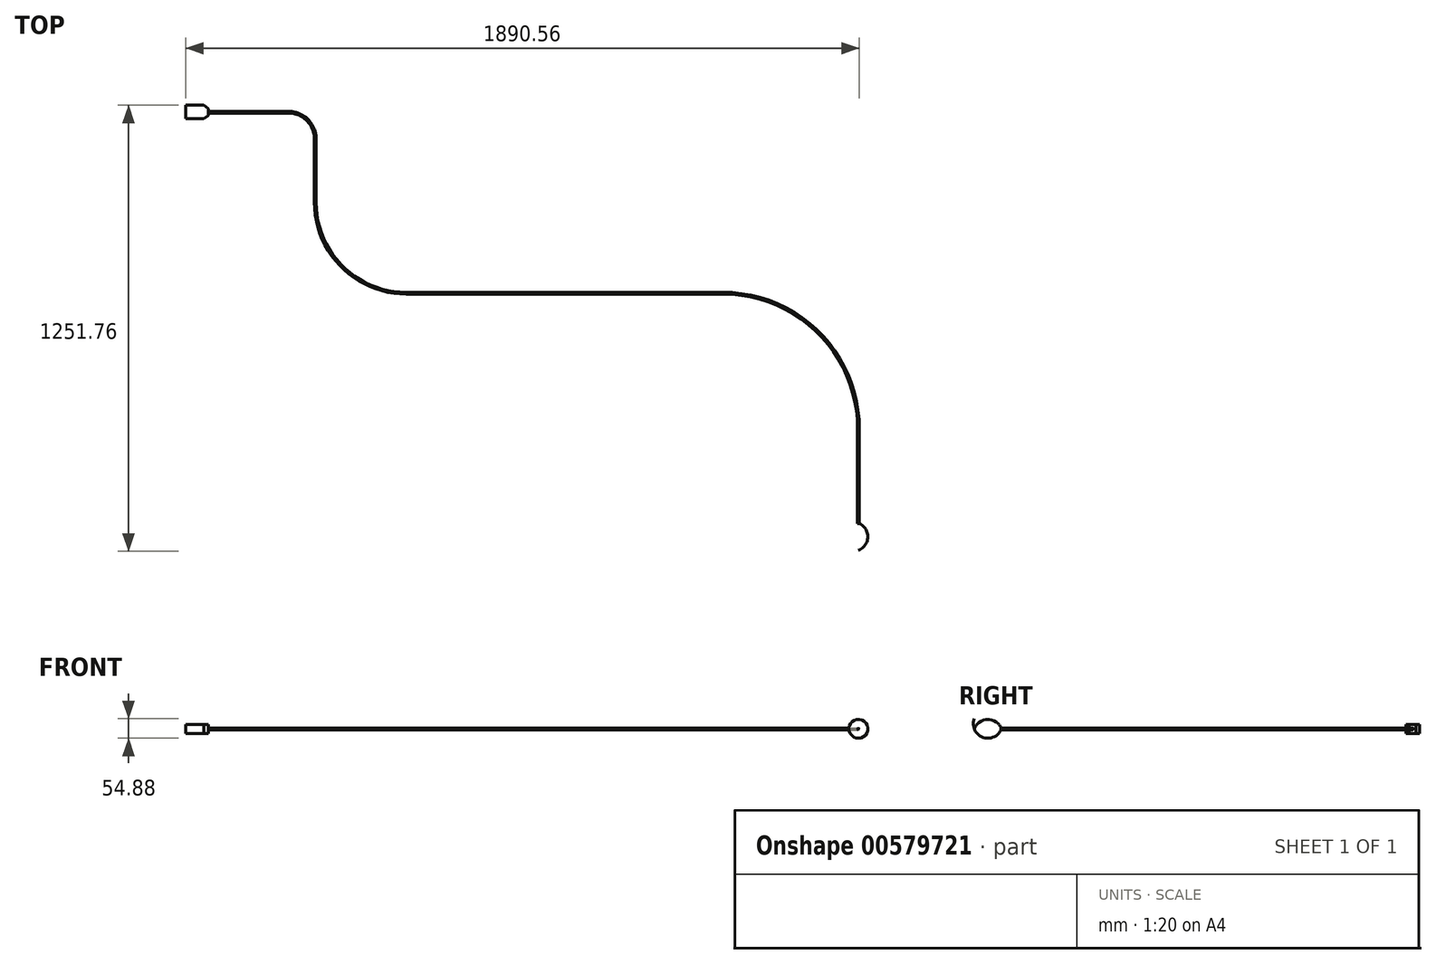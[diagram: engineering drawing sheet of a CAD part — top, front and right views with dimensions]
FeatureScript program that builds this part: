
annotation { "Feature Type Name" : "Feature", "Feature Type Description" : "" }
export const myFeature = defineFeature(function(context is Context, id is Id, definition is map)
    precondition{}
    {
        {
            var Q0;
            Q0=qCreatedBy(makeId("Top.planeOp"),FACE);
            var sketch = newSketch(context, id + "F0", { "sketchPlane" : qUnion([Q0])});
            skLineSegment(sketch, "E0", {"start": v(0, 0) * mm, "end": v(0, -38.1) * mm});
            skLineSegment(sketch, "E1", {"start": v(0, -38.1) * mm, "end": v(50.8, -38.1) * mm});
            skLineSegment(sketch, "E2", {"start": v(0, 0) * mm, "end": v(50.8, 0) * mm});
            skLineSegment(sketch, "E3", {"start": v(50.8, -38.1) * mm, "end": v(64.21, -28.7) * mm});
            skLineSegment(sketch, "E4", {"start": v(50.8, 0) * mm, "end": v(64.21, -9.4) * mm});
            skLineSegment(sketch, "E5", {"start": v(64.21, -28.7) * mm, "end": v(64.21, -9.4) * mm});
            skSolve(sketch);
        }
        {
            var Q0;
            Q0=makeQuery(id+"F0.imprint","IMPRINT",FACE,{"disambiguationData":[TD([[makeQuery(id+"F0.imprint","IMPRINT",EDGE,{"derivedFrom":sQuery(id+"F0.wireOp",EDGE,"E0")}),1.0]])]});
            extrude(context, id + "F1", {"entities" : qUnion([Q0]), "endBound" : BoundingType.SYMMETRIC, "depth" : 25.4 * mm, "offsetDistance" : 25.4 * mm});
        }
        {
            var Q0;
            Q0=makeQuery(id+"F1.opExtrude","SWEPT_FACE",FACE,{"disambiguationData":[OSD([sQuery(id+"F0.wireOp",EDGE,"E5")])]});
            var sketch = newSketch(context, id + "F2", { "sketchPlane" : qUnion([Q0])});
            skSolve(sketch);
        }
        {
            var Q0;
            {var subQ0=sQuery(id+"F0.wireOp",EDGE,"E5");Q0=makeQuery(id+"F2.imprint","IMPRINT",FACE,{"disambiguationData":[TD([[makeQuery(id+"F2.imprint","IMPRINT",EDGE,{"derivedFrom":makeQuery(id+"F1.opExtrude","CAP_EDGE",EDGE,{"disambiguationData":[OSD([subQ0])],"isStart":true})}),1.0]])]});}
            var sketch = newSketch(context, id + "F3", { "sketchPlane" : qUnion([Q0])});
            skCircle(sketch, "E6", {"center": v(-19.42, 0) * mm, "radius": 2.54 * mm});
            skSolve(sketch);
        }
        {
            var Q0;
            Q0=qCreatedBy(makeId("Top.planeOp"),FACE);
            var sketch = newSketch(context, id + "F4", { "sketchPlane" : qUnion([Q0])});
            skLineSegment(sketch, "E7", {"start": v(48.35, -18.45) * mm, "end": v(110.99, -18.45) * mm});
            skLineSegment(sketch, "E8", {"start": v(110.99, -18.45) * mm, "end": v(288.79, -18.45) * mm});
            skLineSegment(sketch, "E9", {"start": v(364.99, -94.65) * mm, "end": v(364.99, -272.45) * mm});
            skLineSegment(sketch, "E10", {"start": v(618.99, -526.45) * mm, "end": v(1507.99, -526.45) * mm});
            skLineSegment(sketch, "E11", {"start": v(1888.99, -907.45) * mm, "end": v(1888.99, -1186.85) * mm});
            skPoint(sketch, "E12.visualSharp", {"position": v(364.99, -18.45) * mm});
            skArc(sketch, "E12.filletArc", {"start": v(364.99, -94.65) * mm, "mid": v(342.67, -40.76) * mm, "end": v(288.79, -18.45) * mm});
            skPoint(sketch, "E13.visualSharp", {"position": v(364.99, -526.45) * mm});
            skArc(sketch, "E13.filletArc", {"start": v(364.99, -272.45) * mm, "mid": v(439.38, -452.05) * mm, "end": v(618.99, -526.45) * mm});
            skPoint(sketch, "E14.visualSharp", {"position": v(1888.99, -526.45) * mm});
            skArc(sketch, "E14.filletArc", {"start": v(1888.99, -907.45) * mm, "mid": v(1777.4, -638.04) * mm, "end": v(1507.99, -526.45) * mm});
            skSolve(sketch);
        }
        {
            var Q0;
            Q0 = qSketchRegion(id + "F3", true);
            var Q1;
            Q1 = qConstructionFilter(qBodyType(qCreatedBy(id + "F4" ,EDGE), BodyType.WIRE), ConstructionObject.NO);
            sweep(context, id + "F5", {"operationType" : NewBodyOperationType.ADD, "profiles" : qUnion([Q0]), "path" : qUnion([Q1])});
        }
        {
            var Q0;
            Q0=qCreatedBy(makeId("Top.planeOp"),FACE);
            var sketch = newSketch(context, id + "F6", { "sketchPlane" : qUnion([Q0])});
            skLineSegment(sketch, "E15", {"start": v(1887.96, -1173) * mm, "end": v(1887.96, -1249.2) * mm});
            skArc(sketch, "E16", {"start": v(1887.96, -1173) * mm, "mid": v(1861.5, -1211.1) * mm, "end": v(1887.96, -1249.2) * mm});
            skSolve(sketch);
        }
        {
            var Q0;
            Q0=makeQuery(id+"F6.imprint","IMPRINT",FACE,{"disambiguationData":[TD([[makeQuery(id+"F6.imprint","IMPRINT",EDGE,{"derivedFrom":sQuery(id+"F6.wireOp",EDGE,"E15")}),-1.0]])]});
            var Q1;
            Q1=sQuery(id+"F6.wireOp",EDGE,"E15");
            revolve(context, id + "F7", {"operationType" : NewBodyOperationType.ADD, "entities" : qUnion([Q0]), "axis" : qUnion([Q1]), "revolveType" : RevolveType.FULL});
        }
    });
